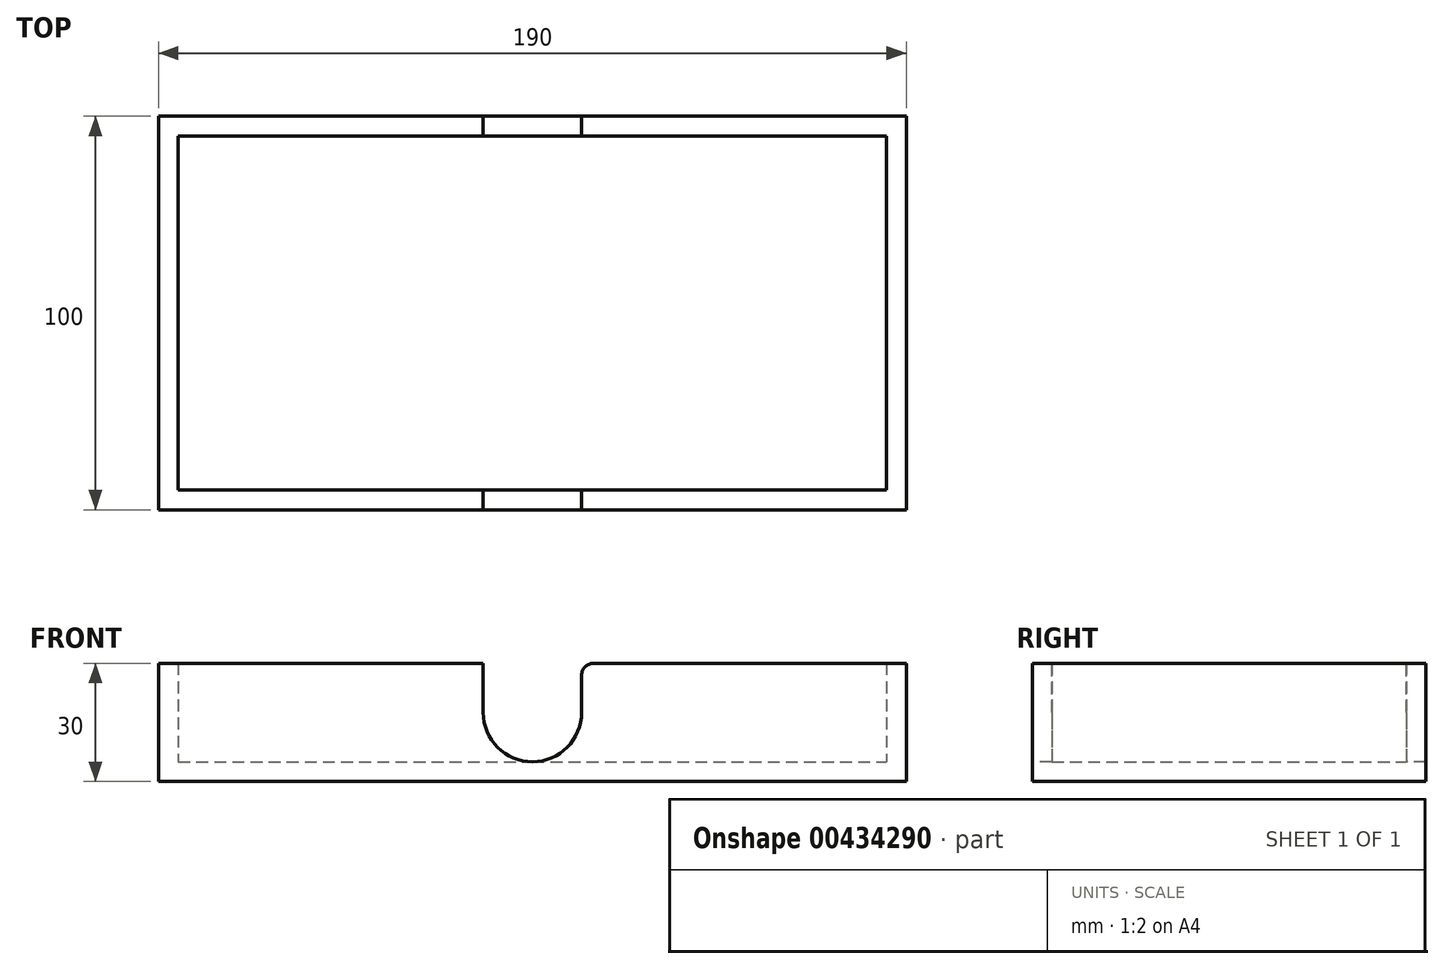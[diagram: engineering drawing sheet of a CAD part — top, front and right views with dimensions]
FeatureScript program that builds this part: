
annotation { "Feature Type Name" : "Feature", "Feature Type Description" : "" }
export const myFeature = defineFeature(function(context is Context, id is Id, definition is map)
    precondition{}
    {
        {
            var Q0;
            Q0=qCreatedBy(makeId("Top.planeOp"),FACE);
            var sketch = newSketch(context, id + "F0", { "sketchPlane" : qUnion([Q0])});
            skLineSegment(sketch, "E0.bottom", {"start": v(-95, -50) * mm, "end": v(95, -50) * mm});
            skLineSegment(sketch, "E0.top", {"start": v(-95, 50) * mm, "end": v(95, 50) * mm});
            skLineSegment(sketch, "E0.left", {"start": v(-95, -50) * mm, "end": v(-95, 50) * mm});
            skLineSegment(sketch, "E0.right", {"start": v(95, -50) * mm, "end": v(95, 50) * mm});
            skPoint(sketch, "E0.middle", {"position": v(0, 0) * mm});
            skSolve(sketch);
        }
        {
            var Q0;
            Q0 = qSketchRegion(id + "F0", true);
            extrude(context, id + "F1", {"entities" : qUnion([Q0]), "depth" : 30 * mm});
        }
        {
            var Q0;
            Q0=makeQuery(id+"F1.opExtrude","CAP_FACE",FACE,{"disambiguationData":[OSD([sQuery(id+"F0.wireOp",EDGE,"E0.bottom"),sQuery(id+"F0.wireOp",EDGE,"E0.top"),sQuery(id+"F0.wireOp",EDGE,"E0.left"),sQuery(id+"F0.wireOp",EDGE,"E0.right")])],"isStart":false});
            shell(context, id + "F2", {"entities" : qUnion([Q0]), "thickness" : 5 * mm});
        }
        {
            var Q0;
            Q0=makeQuery(id+"F1.opExtrude","SWEPT_FACE",FACE,{"disambiguationData":[OSD([sQuery(id+"F0.wireOp",EDGE,"E0.bottom")])]});
            var sketch = newSketch(context, id + "F3", { "sketchPlane" : qUnion([Q0])});
            skCircle(sketch, "E1", {"center": v(0, 17.5) * mm, "radius": 12.5 * mm});
            skLineSegment(sketch, "E2.bottom", {"start": v(-12.5, 30) * mm, "end": v(12.5, 30) * mm});
            skLineSegment(sketch, "E2.top", {"start": v(-12.5, 5) * mm, "end": v(12.5, 5) * mm});
            skLineSegment(sketch, "E2.left", {"start": v(-12.5, 30) * mm, "end": v(-12.5, 5) * mm});
            skLineSegment(sketch, "E2.right", {"start": v(12.5, 30) * mm, "end": v(12.5, 5) * mm});
            skLineSegment(sketch, "E3", {"start": v(-12.5, 17.5) * mm, "end": v(12.5, 17.5) * mm});
            skSolve(sketch);
        }
        {
            var Q0;
            {var subQ0=sQuery(id+"F3.wireOp",EDGE,"E3");Q0=makeQuery(id+"F3.imprint","IMPRINT",FACE,{"disambiguationData":[TD([[makeQuery(id+"F3.imprint","IMPRINT",EDGE,{"derivedFrom":subQ0}),-1.0]])]});}
            var Q1;
            {var subQ1=sQuery(id+"F3.wireOp",EDGE,"E1");var subQ3=sQuery(id+"F3.wireOp",EDGE,"E2.bottom");var subQ4=makeQuery(id+"F3.imprint","INTERSECT",VERTEX,{"derivedFrom":[subQ1,subQ3]});Q1=makeQuery(id+"F3.imprint","IMPRINT",FACE,{"disambiguationData":[TD([[makeQuery(id+"F3.imprint","IMPRINT",EDGE,{"disambiguationData":[TD([[subQ4,-1.0]])],"derivedFrom":subQ1}),-1.0]])]});}
            var Q2;
            {var subQ0=sQuery(id+"F3.wireOp",EDGE,"E3");Q2=makeQuery(id+"F3.imprint","IMPRINT",FACE,{"disambiguationData":[TD([[makeQuery(id+"F3.imprint","IMPRINT",EDGE,{"derivedFrom":subQ0}),1.0]])]});}
            var Q3;
            {var subQ1=sQuery(id+"F3.wireOp",EDGE,"E1");var subQ3=sQuery(id+"F3.wireOp",EDGE,"E2.bottom");var subQ4=makeQuery(id+"F3.imprint","INTERSECT",VERTEX,{"derivedFrom":[subQ1,subQ3]});Q3=makeQuery(id+"F3.imprint","IMPRINT",FACE,{"disambiguationData":[TD([[makeQuery(id+"F3.imprint","IMPRINT",EDGE,{"disambiguationData":[TD([[subQ4,1.0]])],"derivedFrom":subQ1}),-1.0]])]});}
            var Q4;
            Q4=makeQuery(id+"F1.opExtrude","SWEPT_FACE",FACE,{"disambiguationData":[OSD([sQuery(id+"F0.wireOp",EDGE,"E0.top")])]});
            extrude(context, id + "F4", {"entities" : qUnion([Q0, Q1, Q2, Q3]), "operationType" : NewBodyOperationType.REMOVE, "endBound" : BoundingType.UP_TO_SURFACE, "oppositeDirection" : true, "endBoundEntityFace" : qUnion([Q4]), "depth" : 25 * mm});
        }
        {
            var Q0;
            {var subQ0=sQuery(id+"F0.wireOp",EDGE,"E0.bottom");var subQ1=sQuery(id+"F3.wireOp",EDGE,"E2.left");Q0=makeQuery(id+"F4.boolean.opBoolean","COPY",EDGE,{"disambiguationData":[TD([makeQuery(id+"F1.opExtrude","SWEPT_FACE",FACE,{"disambiguationData":[OSD([subQ0])]})])],"derivedFrom":makeQuery(id+"F4.opExtrude","SWEPT_EDGE",EDGE,{"disambiguationData":[OSD([subQ0,sQuery(id+"F3.wireOp",EDGE,"E2.bottom"),subQ1])]})});}
            var Q1;
            {var subQ0=sQuery(id+"F0.wireOp",EDGE,"E0.bottom");var subQ1=sQuery(id+"F3.wireOp",EDGE,"E2.right");Q1=makeQuery(id+"F4.boolean.opBoolean","COPY",EDGE,{"disambiguationData":[TD([makeQuery(id+"F1.opExtrude","SWEPT_FACE",FACE,{"disambiguationData":[OSD([subQ0])]})])],"derivedFrom":makeQuery(id+"F4.opExtrude","SWEPT_EDGE",EDGE,{"disambiguationData":[OSD([subQ0,sQuery(id+"F3.wireOp",EDGE,"E2.bottom"),subQ1])]})});}
            var Q2;
            {var subQ0=sQuery(id+"F0.wireOp",EDGE,"E0.top");var subQ1=sQuery(id+"F0.wireOp",EDGE,"E0.bottom");var subQ2=sQuery(id+"F3.wireOp",EDGE,"E2.left");Q2=makeQuery(id+"F4.boolean.opBoolean","COPY",EDGE,{"disambiguationData":[TD([makeQuery(id+"F1.opExtrude","SWEPT_FACE",FACE,{"disambiguationData":[OSD([subQ0])]})])],"derivedFrom":makeQuery(id+"F4.opExtrude","SWEPT_EDGE",EDGE,{"disambiguationData":[OSD([subQ1,sQuery(id+"F3.wireOp",EDGE,"E2.bottom"),subQ2])]})});}
            var Q3;
            {var subQ0=sQuery(id+"F0.wireOp",EDGE,"E0.top");var subQ1=sQuery(id+"F0.wireOp",EDGE,"E0.bottom");var subQ2=sQuery(id+"F3.wireOp",EDGE,"E2.right");Q3=makeQuery(id+"F4.boolean.opBoolean","COPY",EDGE,{"disambiguationData":[TD([makeQuery(id+"F1.opExtrude","SWEPT_FACE",FACE,{"disambiguationData":[OSD([subQ0])]})])],"derivedFrom":makeQuery(id+"F4.opExtrude","SWEPT_EDGE",EDGE,{"disambiguationData":[OSD([subQ1,sQuery(id+"F3.wireOp",EDGE,"E2.bottom"),subQ2])]})});}
            fillet(context, id + "F5", {"entities" : qUnion([Q0, Q1, Q2, Q3]), "radius" : 3 * mm, "tangentPropagation" : true, "allowEdgeOverflow" : false});
        }
    });
